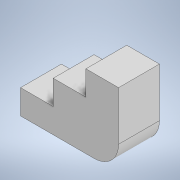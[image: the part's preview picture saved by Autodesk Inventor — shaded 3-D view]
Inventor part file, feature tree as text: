
AUTODESK INVENTOR PART (.ipt)
format: ipt  version: 2022 (Build 260153000, 153)  size: 102,400 bytes
history: native  units: mm
features: other x1, extrude x1, sketch x1
ambient origin geometry x8: Origin, YZ Plane, XZ Plane, XY Plane, X Axis, Y Axis, Z Axis, Center Point
bodies: Body1 (feature_tree)
feature tree (3):
  other  "Sólido1"
  extrude  "Extrusão1"  Depth=15.0mm
  sketch  "Esboço1"  dims[d0=60.0mm d1=15.0mm d2=45.0mm d3=20.0mm d5=20.0mm d6=15.0mm d7=15.0mm d9=20.0mm d11=25.0mm d12=0.0mm]
